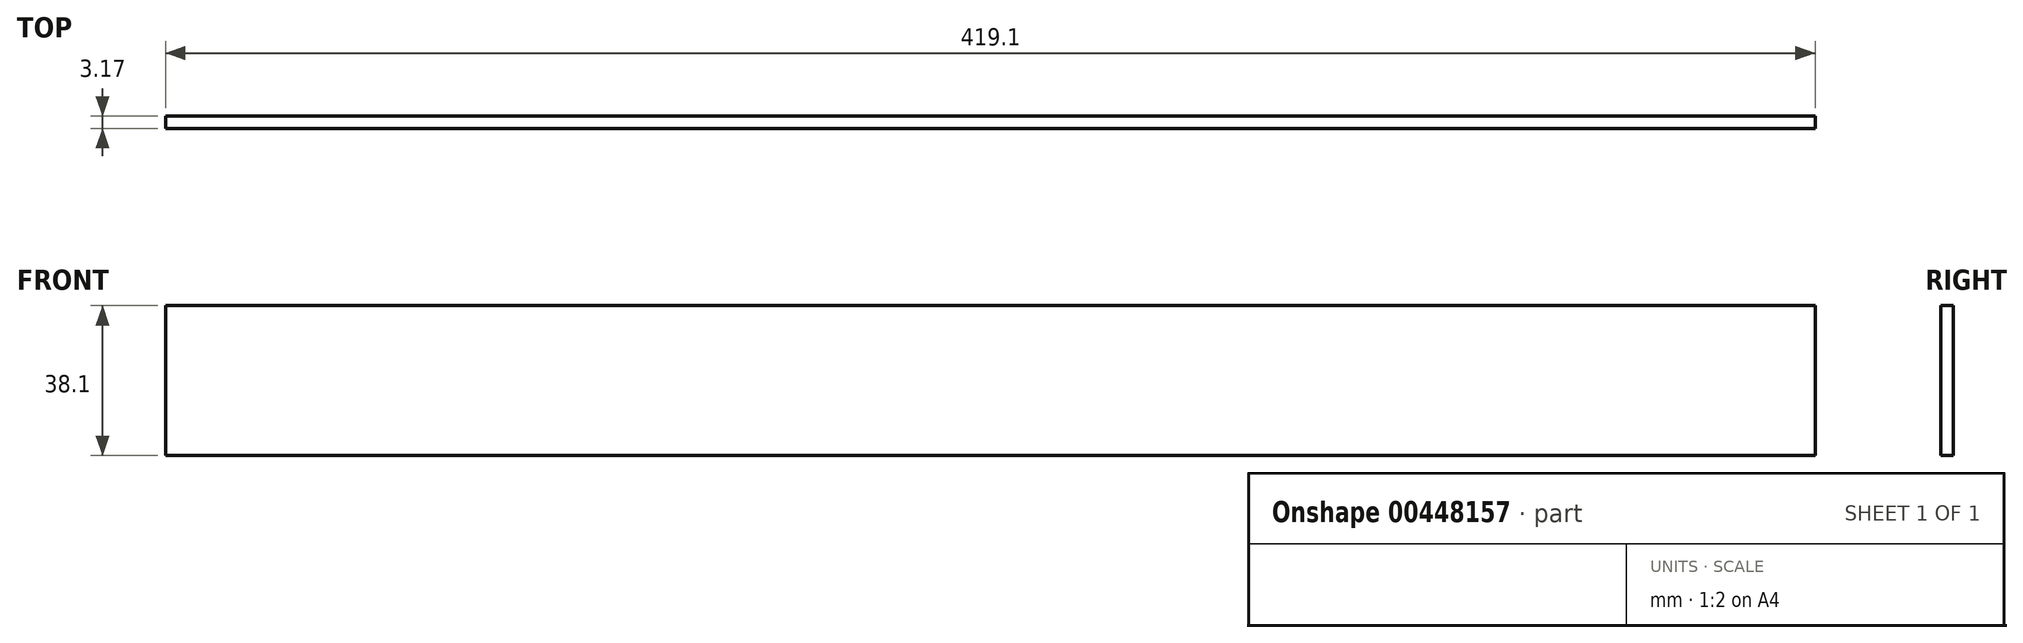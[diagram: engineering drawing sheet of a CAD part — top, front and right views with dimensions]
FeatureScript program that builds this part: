
annotation { "Feature Type Name" : "Feature", "Feature Type Description" : "" }
export const myFeature = defineFeature(function(context is Context, id is Id, definition is map)
    precondition{}
    {
        {
            var Q0;
            Q0=qCreatedBy(makeId("Front.planeOp"),FACE);
            var sketch = newSketch(context, id + "F0", { "sketchPlane" : qUnion([Q0])});
            skLineSegment(sketch, "E0.bottom", {"start": v(-358.01, 28.7) * mm, "end": v(61.09, 28.7) * mm});
            skLineSegment(sketch, "E0.top", {"start": v(-358.01, -9.4) * mm, "end": v(61.09, -9.4) * mm});
            skLineSegment(sketch, "E0.left", {"start": v(-358.01, 28.7) * mm, "end": v(-358.01, -9.4) * mm});
            skLineSegment(sketch, "E0.right", {"start": v(61.09, 28.7) * mm, "end": v(61.09, -9.4) * mm});
            skSolve(sketch);
        }
        {
            var Q0;
            Q0=makeQuery(id+"F0.imprint","IMPRINT",FACE,{"disambiguationData":[TD([[makeQuery(id+"F0.imprint","IMPRINT",EDGE,{"derivedFrom":sQuery(id+"F0.wireOp",EDGE,"E0.bottom")}),-1.0]])]});
            extrude(context, id + "F1", {"entities" : qUnion([Q0]), "depth" : 3.17 * mm});
        }
    });
